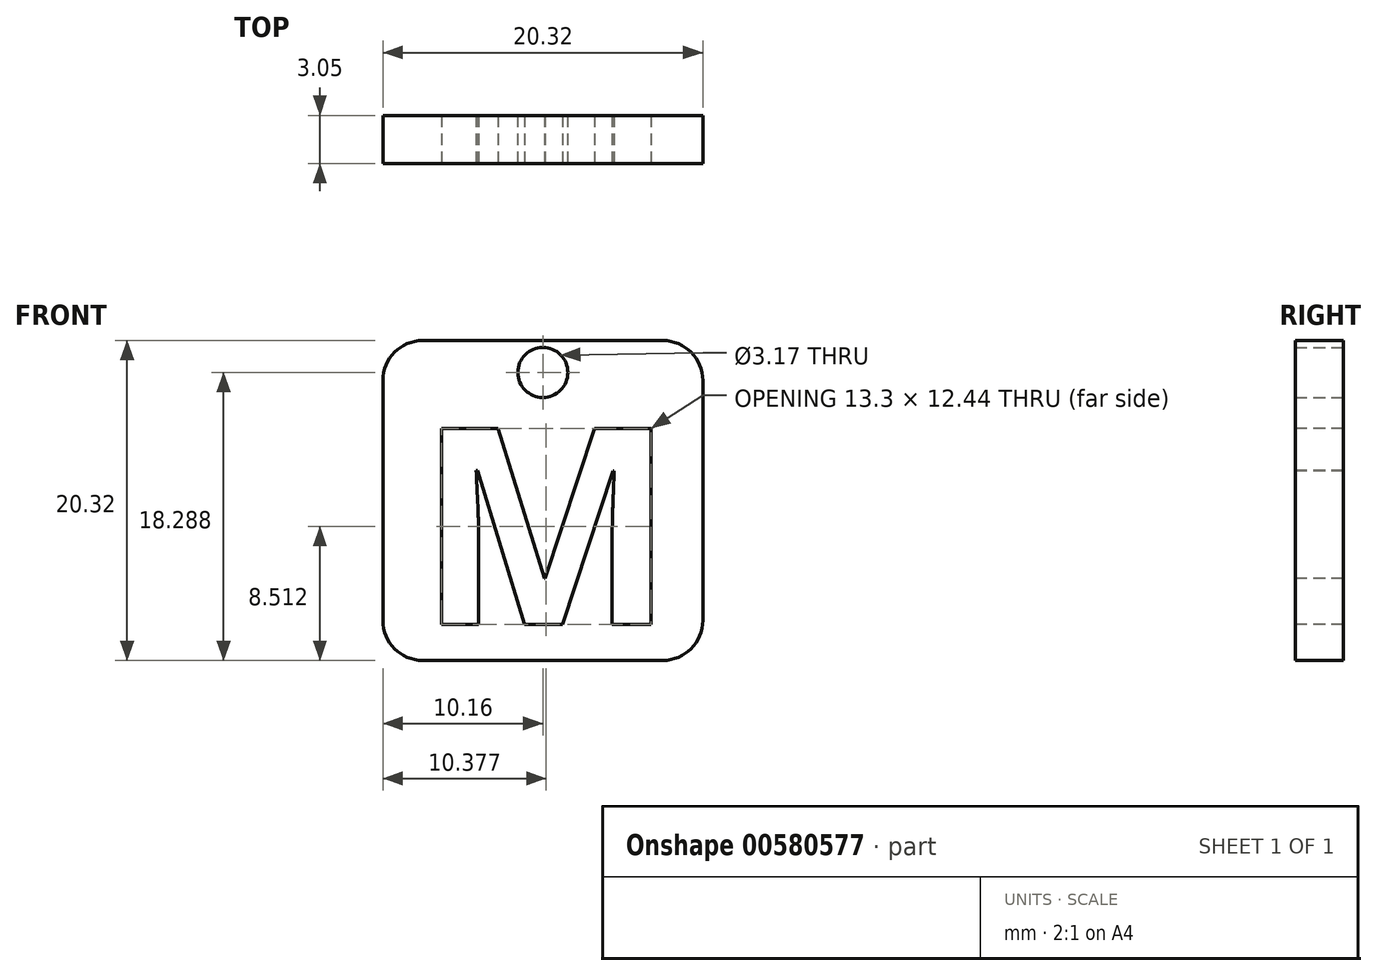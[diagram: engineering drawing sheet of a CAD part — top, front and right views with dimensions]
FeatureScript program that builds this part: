
annotation { "Feature Type Name" : "Feature", "Feature Type Description" : "" }
export const myFeature = defineFeature(function(context is Context, id is Id, definition is map)
    precondition{}
    {
        {
            var Q0;
            Q0=qCreatedBy(makeId("Front.planeOp"),FACE);
            var sketch = newSketch(context, id + "F0", { "sketchPlane" : qUnion([Q0])});
            skLineSegment(sketch, "E0", {"start": v(0, 0) * mm, "end": v(0, 20.32) * mm});
            skLineSegment(sketch, "E1", {"start": v(0, 20.32) * mm, "end": v(20.32, 20.32) * mm});
            skLineSegment(sketch, "E2", {"start": v(20.32, 20.32) * mm, "end": v(20.32, 0) * mm});
            skLineSegment(sketch, "E3", {"start": v(20.32, 0) * mm, "end": v(0, 0) * mm});
            skSolve(sketch);
        }
        {
            var Q0;
            Q0=makeQuery(id+"F0.imprint","IMPRINT",FACE,{"disambiguationData":[TD([[makeQuery(id+"F0.imprint","IMPRINT",EDGE,{"derivedFrom":sQuery(id+"F0.wireOp",EDGE,"E0")}),-1.0]])]});
            extrude(context, id + "F1", {"entities" : qUnion([Q0]), "depth" : 3.05 * mm, "offsetDistance" : 25.4 * mm});
        }
        {
            var Q0;
            Q0=makeQuery(id+"F1.opExtrude","SWEPT_EDGE",EDGE,{"disambiguationData":[OSD([sQuery(id+"F0.wireOp",EDGE,"E1"),sQuery(id+"F0.wireOp",EDGE,"E2")])]});
            var Q1;
            Q1=makeQuery(id+"F1.opExtrude","SWEPT_EDGE",EDGE,{"disambiguationData":[OSD([sQuery(id+"F0.wireOp",EDGE,"E0"),sQuery(id+"F0.wireOp",EDGE,"E3")])]});
            var Q2;
            Q2=makeQuery(id+"F1.opExtrude","SWEPT_EDGE",EDGE,{"disambiguationData":[OSD([sQuery(id+"F0.wireOp",EDGE,"E0"),sQuery(id+"F0.wireOp",EDGE,"E1")])]});
            var Q3;
            Q3=makeQuery(id+"F1.opExtrude","SWEPT_EDGE",EDGE,{"disambiguationData":[OSD([sQuery(id+"F0.wireOp",EDGE,"E2"),sQuery(id+"F0.wireOp",EDGE,"E3")])]});
            fillet(context, id + "F2", {"entities" : qUnion([Q0, Q1, Q2, Q3]), "radius" : 2.54 * mm, "tangentPropagation" : true, "allowEdgeOverflow" : false});
        }
        {
            var Q0;
            Q0=qCreatedBy(makeId("Front.planeOp"),FACE);
            var sketch = newSketch(context, id + "F3", { "sketchPlane" : qUnion([Q0])});
            skCircle(sketch, "E4", {"center": v(10.16, 18.29) * mm, "radius": 1.59 * mm});
            skSolve(sketch);
        }
        {
            var Q0;
            Q0=qCreatedBy(makeId("Front.planeOp"),FACE);
            cPlane(context, id + "F4", {"entities" : qUnion([Q0]), "cplaneType" : CPlaneType.OFFSET, "offset" : 25.4 * mm, "width" : 152.4 * mm, "height" : 152.4 * mm});
        }
        {
            var Q0;
            Q0 = qSketchRegion(id + "F3", true);
            extrude(context, id + "F5", {"entities" : qUnion([Q0]), "operationType" : NewBodyOperationType.REMOVE, "depth" : 25.4 * mm, "offsetDistance" : 25.4 * mm});
        }
        {
            var Q0;
            Q0=qCreatedBy(id+"F4.planeOp",FACE);
            var sketch = newSketch(context, id + "F6", { "sketchPlane" : qUnion([Q0])});
            skText(sketch, "E5", { "text": "M", "fontName": "OpenSans-Bold.ttf"});
            const initialGuessF6  = {"E5": [0.00216, 0.00229, 1, 0, 0.01255]};
            skSetInitialGuess(sketch, initialGuessF6);
            skSolve(sketch);
        }
        {
            var Q0;
            Q0 = qSketchRegion(id + "F6", true);
            extrude(context, id + "F7", {"entities" : qUnion([Q0]), "operationType" : NewBodyOperationType.REMOVE, "oppositeDirection" : true, "depth" : 25.4 * mm, "offsetDistance" : 25.4 * mm});
        }
    });
